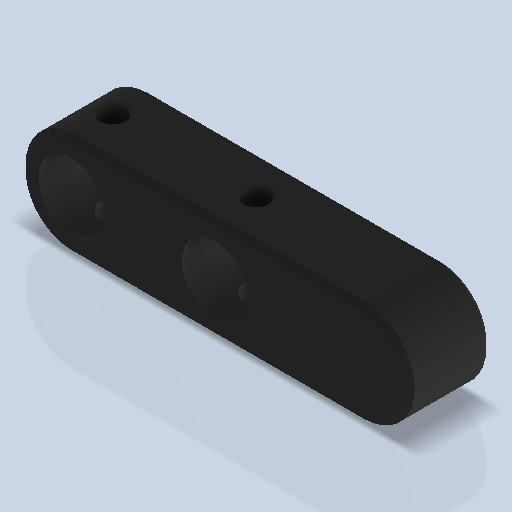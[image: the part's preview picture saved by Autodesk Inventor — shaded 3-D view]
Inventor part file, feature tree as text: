
AUTODESK INVENTOR PART (.ipt)
format: ipt  version: 2024.2 (Build 282272000, 272)  size: 275,968 bytes
history: native  units: mm
features: sketch x4, hole x3, extrude x1, chamfer x1
ambient origin geometry x8: Origin, YZ Plane, XZ Plane, XY Plane, X Axis, Y Axis, Z Axis, Center Point
bodies: Volumenkörper1 (feature_tree)
feature tree (9):
  extrude  "Extrusion1"  Depth=38.0mm
  hole  "Bohrung2"  [1 undecoded]
  chamfer  "Fasen1"  Distance=0.5mm Angle=45.0deg
  hole  "Bohrung1"  [1 undecoded]
  hole  "Bohrung3"  [1 undecoded]
  sketch  "Skizze1"  dims[d0=10.0mm d1=38.0mm]
  sketch  "Skizze2"  dims[d2=8.0mm d3=0.0mm]
  sketch  "Skizze3"  dims[d4=6.5mm d5=6.0mm d6=4.0mm d7=2.0mm d8=90.0deg d9=8.0mm d10=20.594885mm]
  sketch  "Skizze4"  dims[d11=6.5mm d12=6.0mm d13=4.0mm d14=2.0mm d15=90.0deg d16=8.0mm d17=0.0mm d18=2.5mm d19=6.0mm d20=4.0mm d21=2.0mm d22=90.0deg d23=8.0mm d24=0.0mm d25=4.0mm d27=0.5mm d28=2.0mm d29=45.0deg]
note: 3 required parameter values undecoded (feature->parameter linkage not recoverable at this tier; creation-order binding heuristic only, values carry confidence <= 0.55)
